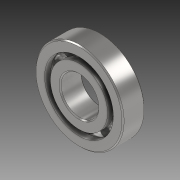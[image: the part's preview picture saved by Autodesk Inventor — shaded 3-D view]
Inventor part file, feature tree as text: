
AUTODESK INVENTOR PART (.ipt)
format: ipt  version: 2020 (Build 240168000, 168)  size: 471,040 bytes
history: mixed  units: in
note: dims shown in document units (in); Inventor stores cm internally (conversion verified against a paired STEP export)
features: other x9, revolve x3, imported_body x1
ambient origin geometry x8: Origin, YZ Plane, XZ Plane, XY Plane, X Axis, Y Axis, Z Axis, Center Point
bodies: Solid1 (imported_parasolid), Solid2 (imported_parasolid), Solid3 (imported_parasolid), Solid4 (imported_parasolid), Solid5 (imported_parasolid), Solid6 (imported_parasolid), Solid7 (imported_parasolid), Solid8 (imported_parasolid), Solid9 (imported_parasolid), Solid10 (imported_parasolid), Solid11 (imported_parasolid), Solid12 (imported_parasolid)
feature tree (13):
  revolve  "Revolve1"  [1 undecoded]
  revolve  "Revolve3"  [1 undecoded]
  revolve  "Revolve4"  [1 undecoded]
  other  "CirPattern1[1]"
  other  "CirPattern1[2]"
  other  "CirPattern1[3]"
  other  "CirPattern1[4]"
  other  "CirPattern1[5]"
  other  "CirPattern1[6]"
  other  "CirPattern1[7]"
  other  "CirPattern1[8]"
  other  "CirPattern1[9]"
  imported_body  NMx_Import_Brep_tag  [imported B-rep: ~26 faces, bbox_mm=[6.35, 0.0, 5.55625]]
note: 3 required parameter values undecoded (feature->parameter linkage not recoverable at this tier; creation-order binding heuristic only, values carry confidence <= 0.55)
